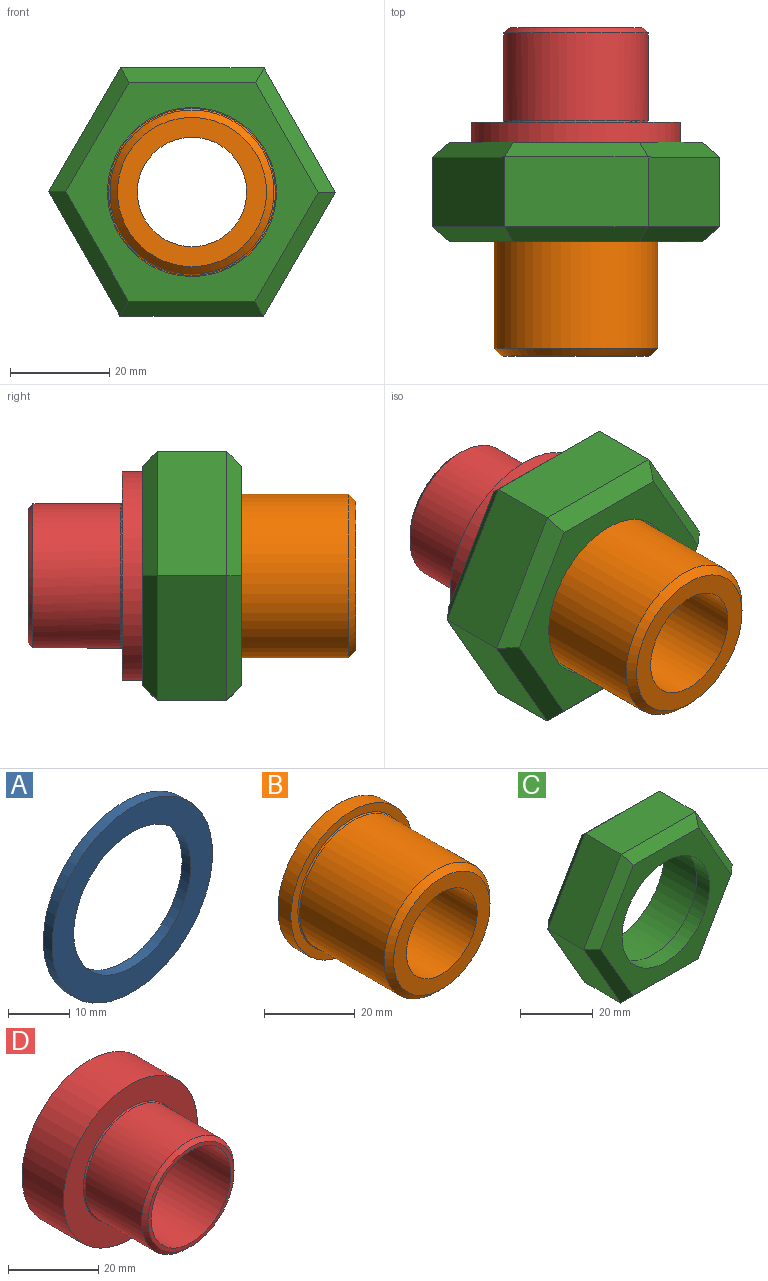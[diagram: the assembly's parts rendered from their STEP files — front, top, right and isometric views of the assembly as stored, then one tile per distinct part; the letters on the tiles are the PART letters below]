
ASSEMBLY  parts=4 mates=6
PART A: 4 faces, bbox 37x2x37 mm
  f0: cylinder r=13.5mm len=27mm, axis (0,-1,0), area 169.6mm2, adj f2,f3
  f1: cylinder r=18.5mm len=37mm, axis (0,-1,0), area 232.5mm2, adj f2,f3
  f2: plane 37x37mm, normal (0,1,0), area 502.7mm2, adj f0,f1
  f3: plane 37x37mm, normal (0,-1,0), area 502.7mm2, adj f0,f1
PART B: 8 faces, bbox 38x32x38 mm
  f0: cylinder r=19mm len=38mm, axis (0,-1,0), area 477.5mm2, adj f1,f3
  f1: plane 38x38mm, normal (0,1,0), area 754mm2, adj f0,f5
  f2: cylinder r=16.5mm len=33mm, axis (0,-1,0), area 2716.2mm2, adj f6,f7
  f3: plane 38x38mm, normal (0,-1,0), area 247.4mm2, adj f0,f7
  f4: plane 30x30mm, normal (0,-1,0), area 326.7mm2, adj f5,f6
  f5: cylinder r=11mm len=32mm, axis (0,-1,0), area 2211.7mm2, adj f1,f4
  f6: cone r=15mm half-angle=45deg, axis (0,1,0), area 209.9mm2, adj f2,f4
  f7: torus R=16.8mm, axis (0,-1,0), area 49.2mm2, adj f2,f3
PART C: 23 faces, bbox 57.7x20x50.1 mm
  f0: cylinder r=19.5mm len=39mm, axis (0,-1,0), area 1837.8mm2, adj f8,f22
  f1: plane 25.04x14.36mm, normal (0.87,0,0.5), area 404.1mm2, adj f2,f6,f13,f15
  f2: plane 28.87x14mm, normal (0,0,1), area 404.1mm2, adj f1,f3,f14,f17
  f3: plane 24.96x14.51mm, normal (-0.86,0,0.5), area 404.1mm2, adj f2,f4,f12,f19
  f4: plane 25.04x14.36mm, normal (-0.87,0,-0.5), area 404.1mm2, adj f3,f5,f10,f20
  f5: plane 28.87x14mm, normal (0,0,-1), area 404.1mm2, adj f4,f6,f9,f18
  f6: plane 24.96x14.51mm, normal (0.86,0,-0.5), area 404.1mm2, adj f1,f5,f11,f16
  f7: plane 50.81x44.08mm, normal (0,-1,0), area 768.7mm2, adj f15,f16,f17,f18,f19,f20,f21
  f8: plane 50.81x44.08mm, normal (0,1,0), area 482mm2, adj f0,f9,f10,f11,f12,f13,f14
  f9: plane 28.87x3.08mm, normal (0,0.71,-0.71), area 115.1mm2, adj f5,f8,f10,f11
  f10: plane 25.04x16.1mm, normal (-0.61,0.71,-0.35), area 115.1mm2, adj f4,f8,f9,f12
  f11: plane 24.97x16.23mm, normal (0.61,0.71,-0.36), area 115.1mm2, adj f6,f8,f9,f13
  f12: plane 24.97x16.23mm, normal (-0.61,0.71,0.36), area 115.1mm2, adj f3,f8,f10,f14
  f13: plane 25.04x16.1mm, normal (0.61,0.71,0.35), area 115.1mm2, adj f1,f8,f11,f14
  f14: plane 28.87x3.08mm, normal (0,0.71,0.71), area 115.1mm2, adj f2,f8,f12,f13
  f15: plane 25.04x16.1mm, normal (0.61,-0.71,0.35), area 115.1mm2, adj f1,f7,f16,f17
  f16: plane 24.97x16.23mm, normal (0.61,-0.71,-0.36), area 115.1mm2, adj f6,f7,f15,f18
  f17: plane 28.87x3.08mm, normal (0,-0.71,0.71), area 115.1mm2, adj f2,f7,f15,f19
  f18: plane 28.87x3.08mm, normal (0,-0.71,-0.71), area 115.1mm2, adj f5,f7,f16,f20
  f19: plane 24.97x16.23mm, normal (-0.61,-0.71,0.36), area 115.1mm2, adj f3,f7,f17,f20
  f20: plane 25.04x16.1mm, normal (-0.61,-0.71,-0.35), area 115.1mm2, adj f4,f7,f18,f19
  f21: cylinder r=17mm len=34mm, axis (0,-1,0), area 534.1mm2, adj f7,f22
  f22: plane 39x39mm, normal (0,1,0), area 286.7mm2, adj f0,f21
PART D: 8 faces, bbox 42x32x42 mm
  f0: cylinder r=14.5mm len=29mm, axis (0,-1,0), area 1612.6mm2, adj f4,f7
  f1: cylinder r=12.5mm len=32mm, axis (0,-1,0), area 2513.3mm2, adj f2,f3
  f2: plane 42x42mm, normal (0,1,0), area 894.6mm2, adj f1,f5
  f3: plane 27x27mm, normal (0,-1,0), area 81.7mm2, adj f1,f4
  f4: cone r=13.5mm half-angle=45deg, axis (0,1,0), area 124.4mm2, adj f0,f3
  f5: cylinder r=21mm len=42mm, axis (0,1,0), area 1715.3mm2, adj f2,f6
  f6: plane 42x42mm, normal (0,-1,0), area 697.3mm2, adj f5,f7
  f7: torus R=14.8mm, axis (0,1,0), area 43.3mm2, adj f0,f6
PLACE A t=(68.26,79.35,11.38)mm
PLACE B t=(68.26,47.35,11.38)mm
PLACE C t=(68.26,90.35,11.38)mm
PLACE D rot(axis=(1,0,0),180deg) t=(68.26,113.35,11.38)mm
MATE cylindrical A.f0 <-> C.f0  axis (0,-1,0) through (68.26,79.35,11.38)mm
MATE planar B.f0 <-> C.f0  axis (0,-1,0) through (68.26,75.35,11.38)mm
MATE cylindrical B.f0 <-> C.f0  axis (0,-1,0) through (68.26,61.95,11.38)mm
MATE planar D.f0 <-> A.f0  axis (0,-1,0) through (68.26,81.35,11.38)mm
MATE cylindrical D.f0 <-> C.f0  axis (0,-1,0) through (68.26,87.85,11.38)mm
MATE planar A.f0 <-> B.f0  axis (0,-1,0) through (68.26,79.35,11.38)mm
